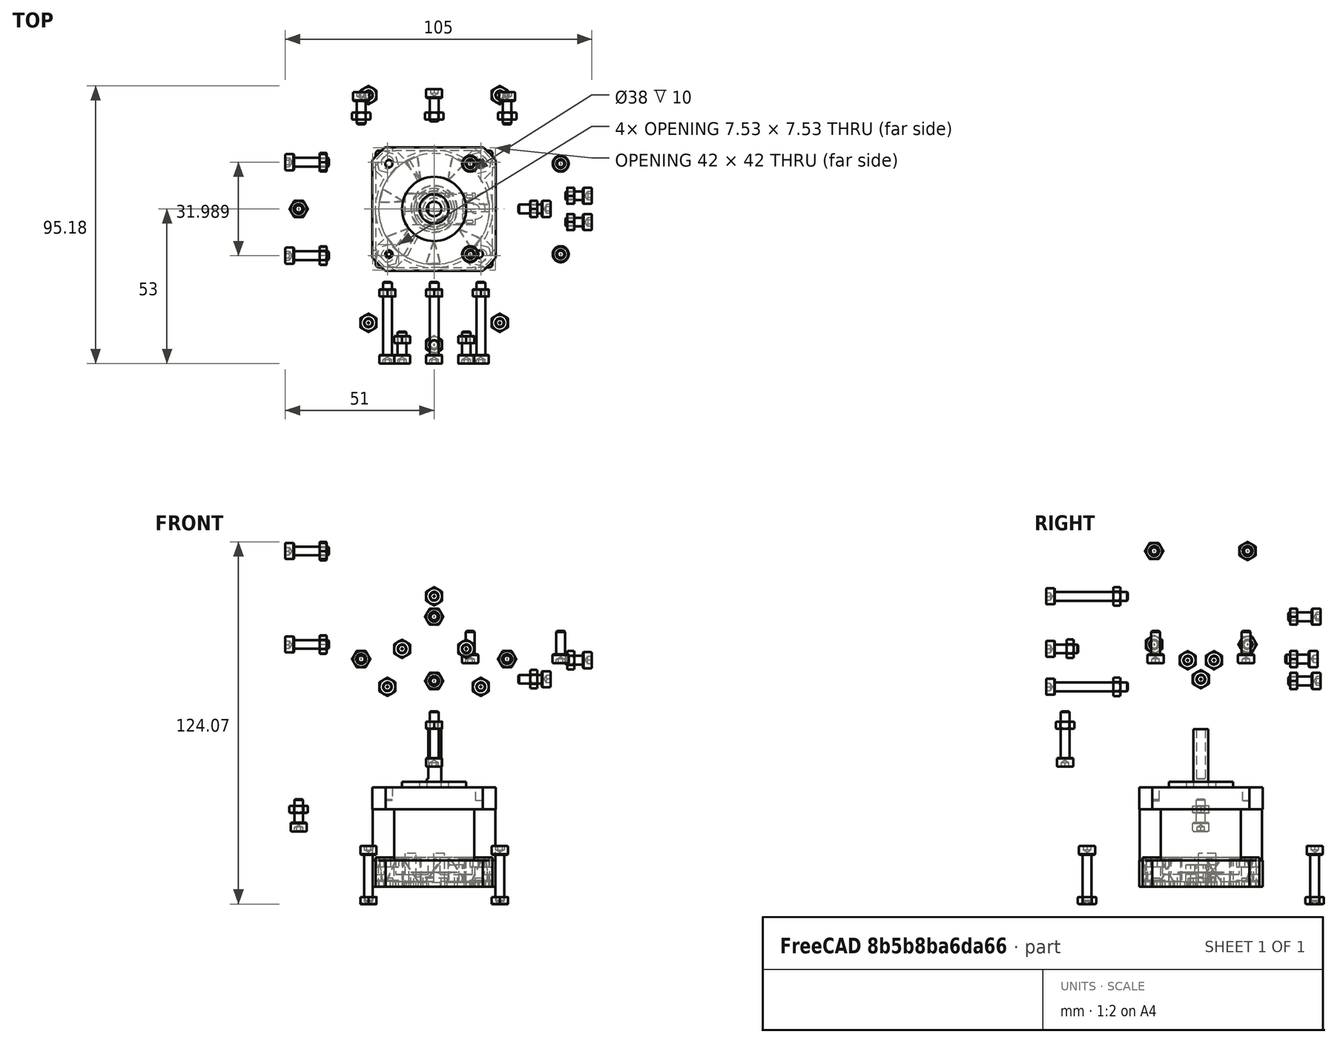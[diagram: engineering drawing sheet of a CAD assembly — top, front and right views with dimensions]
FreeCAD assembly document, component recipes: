
FREECAD ASSEMBLY — COMPONENT RECIPES ("AssemblyArt3")

This assembly document has 5 components, labeled P0..P4 below (a component is one placed body or linked part). 0 of them carry a construction recipe — the FreeCAD feature program that regenerates the part from scratch, quoted from this document or its linked companion documents; the rest are supplied as boundary geometry only. No exploded tour is included for this assembly.
COMPONENT P0 — geometry summary ("Bearing_625ZZ"; no construction recipe available for this part):
  bounding box: 16.0 x 16.0 x 5.0 mm
  tessellated surface: 4,788 triangles
  volume: 876 mm^3 (68% of its bounding box)
  symmetry: 2-fold rotationally symmetric about the x axis; 2-fold rotationally symmetric about the y axis; revolution-symmetric about the z axis through its bounding-box center; mirror-symmetric across its x mid-plane, y mid-plane, z mid-plane
COMPONENT P1 — geometry summary ("Fan_40x40"; no construction recipe available for this part):
  bounding box: 40.0 x 40.0 x 10.0 mm
  tessellated surface: 7,642 triangles
  volume: 6703 mm^3 (42% of its bounding box)
COMPONENT P2 — geometry summary ("OpticSensor"; no construction recipe available for this part):
  bounding box: 27.6 x 11.5 x 11.0 mm
  tessellated surface: 1,248 triangles
  volume: 1247 mm^3 (36% of its bounding box)
COMPONENT P3 — geometry summary ("BearingBalls"; no construction recipe available for this part):
  bounding box: 76.0 x 76.0 x 6.0 mm
  tessellated surface: 288,000 triangles
  volume: 4072 mm^3 (12% of its bounding box)
  symmetry: 2-fold rotationally symmetric about the x axis; 2-fold rotationally symmetric about the y axis; 6-fold rotationally symmetric about the z axis; mirror-symmetric across its x mid-plane, y mid-plane, z mid-plane
COMPONENT P4 — geometry summary ("Stepper_Nema17x34"; no construction recipe available for this part):
  bounding box: 54.0 x 42.3 x 42.3 mm
  tessellated surface: 6,438 triangles
  volume: 58557 mm^3 (61% of its bounding box)
  symmetry: 4-fold rotationally symmetric about the z axis; mirror-symmetric across its x mid-plane, y mid-plane
PROVENANCE & LICENSES
A FreeCAD (.FCStd) document from a public repository crawl; recipes are the document's own serialized feature recipes (and, for linked parts, companion documents' recipes).
License: as declared in the source repository (recorded in the dataset sidecar).
